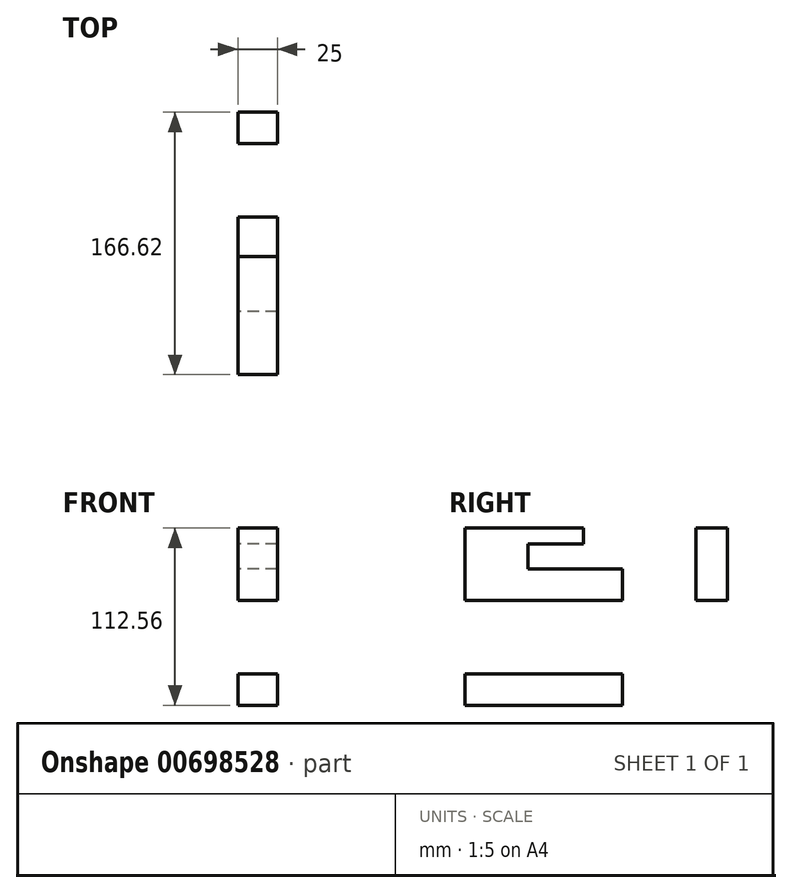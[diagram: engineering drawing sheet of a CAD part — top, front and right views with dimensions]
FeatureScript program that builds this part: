
annotation { "Feature Type Name" : "Feature", "Feature Type Description" : "" }
export const myFeature = defineFeature(function(context is Context, id is Id, definition is map)
    precondition{}
    {
        {
            var Q0;
            Q0=qCreatedBy(makeId("Right.planeOp"),FACE);
            var sketch = newSketch(context, id + "F0", { "sketchPlane" : qUnion([Q0])});
            skLineSegment(sketch, "E0", {"start": v(-554.15, 52.57) * mm, "end": v(-454.15, 52.57) * mm});
            skLineSegment(sketch, "E1", {"start": v(-454.15, 52.57) * mm, "end": v(-454.15, 72.57) * mm});
            skLineSegment(sketch, "E2", {"start": v(-454.15, 72.57) * mm, "end": v(-514.15, 72.57) * mm});
            skLineSegment(sketch, "E3", {"start": v(-514.15, 72.57) * mm, "end": v(-514.15, 88.57) * mm});
            skLineSegment(sketch, "E4", {"start": v(-514.15, 88.57) * mm, "end": v(-479.15, 88.57) * mm});
            skLineSegment(sketch, "E5", {"start": v(-479.15, 88.57) * mm, "end": v(-479.15, 98.57) * mm});
            skLineSegment(sketch, "E6", {"start": v(-479.15, 98.57) * mm, "end": v(-554.15, 98.57) * mm});
            skLineSegment(sketch, "E7", {"start": v(-554.15, 98.57) * mm, "end": v(-554.15, 52.57) * mm});
            skLineSegment(sketch, "E8", {"start": v(-554.15, 6) * mm, "end": v(-554.15, -14) * mm});
            skLineSegment(sketch, "E9", {"start": v(-554.15, -14) * mm, "end": v(-454.15, -14) * mm});
            skLineSegment(sketch, "E10", {"start": v(-454.15, -14) * mm, "end": v(-454.15, 6) * mm});
            skLineSegment(sketch, "E11", {"start": v(-454.15, 6) * mm, "end": v(-554.15, 6) * mm});
            skLineSegment(sketch, "E12", {"start": v(-479.15, -14) * mm, "end": v(-479.15, -1.5) * mm});
            skLineSegment(sketch, "E13", {"start": v(-479.15, -1.5) * mm, "end": v(-514.15, -1.5) * mm});
            skLineSegment(sketch, "E14", {"start": v(-514.15, -1.5) * mm, "end": v(-514.15, -14) * mm, "construction": true});
            skLineSegment(sketch, "E15", {"start": v(-514.15, -1.5) * mm, "end": v(-514.15, 6) * mm});
            skLineSegment(sketch, "E16", {"start": v(-407.53, 52.57) * mm, "end": v(-387.53, 52.57) * mm});
            skLineSegment(sketch, "E17", {"start": v(-387.53, 52.57) * mm, "end": v(-387.53, 98.57) * mm});
            skLineSegment(sketch, "E18", {"start": v(-387.53, 98.57) * mm, "end": v(-407.53, 98.57) * mm});
            skLineSegment(sketch, "E19", {"start": v(-407.53, 98.57) * mm, "end": v(-407.53, 52.57) * mm});
            skLineSegment(sketch, "E20", {"start": v(-407.53, 72.57) * mm, "end": v(-387.53, 72.57) * mm, "construction": true});
            skLineSegment(sketch, "E21", {"start": v(-387.53, 88.57) * mm, "end": v(-400.03, 88.57) * mm, "construction": true});
            skLineSegment(sketch, "E22", {"start": v(-400.03, 88.57) * mm, "end": v(-400.03, 98.57) * mm, "construction": true});
            skSolve(sketch);
        }
        {
            var Q0;
            Q0 = qSketchRegion(id + "F0", true);
            extrude(context, id + "F1", {"entities" : qUnion([Q0]), "depth" : 25 * mm, "offsetDistance" : 25 * mm});
        }
    });
